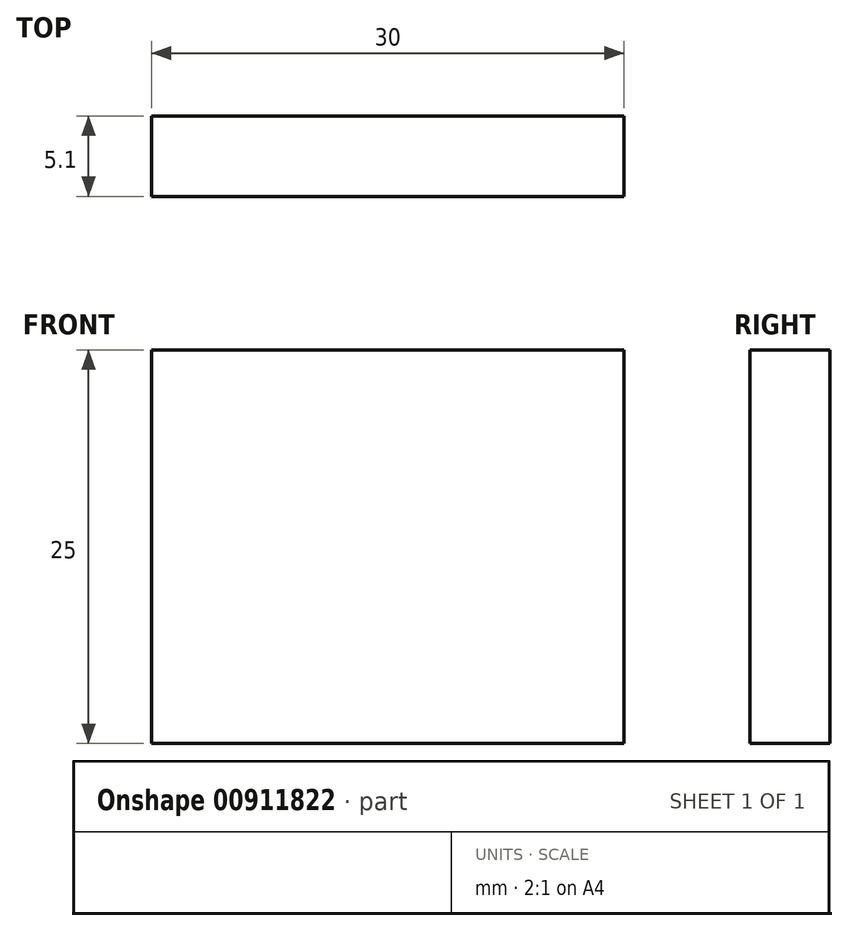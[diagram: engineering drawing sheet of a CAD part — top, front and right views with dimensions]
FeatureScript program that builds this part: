
annotation { "Feature Type Name" : "Feature", "Feature Type Description" : "" }
export const myFeature = defineFeature(function(context is Context, id is Id, definition is map)
    precondition{}
    {
        {
            var Q0;
            Q0=qCreatedBy(makeId("Front.planeOp"),FACE);
            var sketch = newSketch(context, id + "F0", { "sketchPlane" : qUnion([Q0])});
            skLineSegment(sketch, "E0.bottom", {"start": v(-78.93, 62.1) * mm, "end": v(78.93, 62.1) * mm});
            skLineSegment(sketch, "E0.top", {"start": v(-78.93, -62.1) * mm, "end": v(78.93, -62.1) * mm});
            skLineSegment(sketch, "E0.left", {"start": v(-78.93, 62.1) * mm, "end": v(-78.93, -62.1) * mm});
            skLineSegment(sketch, "E0.right", {"start": v(78.93, 62.1) * mm, "end": v(78.93, -62.1) * mm});
            skPoint(sketch, "E0.middle", {"position": v(0, 0) * mm});
            skLineSegment(sketch, "E1.bottom", {"start": v(-167.5, 20) * mm, "end": v(-136.12, 20) * mm});
            skLineSegment(sketch, "E1.top", {"start": v(-167.5, 0) * mm, "end": v(-136.12, 0) * mm});
            skLineSegment(sketch, "E1.left", {"start": v(-167.5, 20) * mm, "end": v(-167.5, 0) * mm});
            skLineSegment(sketch, "E1.right", {"start": v(-136.12, 20) * mm, "end": v(-136.12, 0) * mm});
            skLineSegment(sketch, "E2", {"start": v(-151.81, 20) * mm, "end": v(-151.81, 15) * mm});
            skLineSegment(sketch, "E3", {"start": v(-151.81, 15) * mm, "end": v(-146.81, 15) * mm});
            skLineSegment(sketch, "E4.bottom", {"start": v(-146.81, 15) * mm, "end": v(-151.81, 15) * mm});
            skLineSegment(sketch, "E4.top", {"start": v(-146.81, 5) * mm, "end": v(-151.81, 5) * mm});
            skLineSegment(sketch, "E4.left", {"start": v(-146.81, 15) * mm, "end": v(-146.81, 5) * mm});
            skPoint(sketch, "E5.end.orphan", {"position": v(-146.81, 10) * mm});
            skPoint(sketch, "E6.orphan", {"position": v(-151.81, 10) * mm});
            skPoint(sketch, "E7.end.orphan", {"position": v(-151.81, 0) * mm});
            skLineSegment(sketch, "E8", {"start": v(-151.81, 5) * mm, "end": v(-151.81, 0) * mm});
            skLineSegment(sketch, "E9.right", {"start": v(-134.62, -22.1) * mm, "end": v(-134.62, -42.1) * mm});
            skLineSegment(sketch, "E10", {"start": v(-150.31, -22.1) * mm, "end": v(-150.31, -27.1) * mm});
            skLineSegment(sketch, "E11", {"start": v(-150.31, -27.1) * mm, "end": v(-145.31, -27.1) * mm});
            skLineSegment(sketch, "E12.bottom", {"start": v(-145.31, -27.1) * mm, "end": v(-150.31, -27.1) * mm});
            skLineSegment(sketch, "E12.top", {"start": v(-145.31, -37.1) * mm, "end": v(-150.31, -37.1) * mm});
            skLineSegment(sketch, "E12.left", {"start": v(-145.31, -27.1) * mm, "end": v(-145.31, -37.1) * mm});
            skPoint(sketch, "E13.end.orphan", {"position": v(-145.31, -32.1) * mm});
            skPoint(sketch, "E14.orphan", {"position": v(-150.31, -32.1) * mm});
            skPoint(sketch, "E15.end.orphan", {"position": v(-150.31, -42.1) * mm});
            skLineSegment(sketch, "E16", {"start": v(-150.31, -37.1) * mm, "end": v(-150.31, -42.1) * mm});
            skLineSegment(sketch, "E17.left", {"start": v(-222.13, -12.84) * mm, "end": v(-222.13, -32.84) * mm});
            skLineSegment(sketch, "E18", {"start": v(-206.43, -12.84) * mm, "end": v(-206.43, -17.84) * mm});
            skLineSegment(sketch, "E19", {"start": v(-206.43, -17.84) * mm, "end": v(-201.43, -17.84) * mm});
            skLineSegment(sketch, "E20.bottom", {"start": v(-201.43, -17.84) * mm, "end": v(-206.43, -17.84) * mm});
            skLineSegment(sketch, "E20.top", {"start": v(-201.43, -27.84) * mm, "end": v(-206.43, -27.84) * mm});
            skLineSegment(sketch, "E20.left", {"start": v(-201.43, -17.84) * mm, "end": v(-201.43, -27.84) * mm});
            skPoint(sketch, "E21.end.orphan", {"position": v(-201.43, -22.84) * mm});
            skPoint(sketch, "E22.orphan", {"position": v(-206.43, -22.84) * mm});
            skPoint(sketch, "E23.end.orphan", {"position": v(-206.43, -32.84) * mm});
            skLineSegment(sketch, "E24", {"start": v(-206.43, -27.84) * mm, "end": v(-206.43, -32.84) * mm});
            skLineSegment(sketch, "E25", {"start": v(-222.13, -12.84) * mm, "end": v(-206.43, -12.84) * mm});
            skLineSegment(sketch, "E26", {"start": v(-206.43, -32.84) * mm, "end": v(-222.13, -32.84) * mm});
            skLineSegment(sketch, "E27", {"start": v(-150.31, -22.1) * mm, "end": v(-134.62, -22.1) * mm});
            skLineSegment(sketch, "E28", {"start": v(-150.31, -42.1) * mm, "end": v(-134.62, -42.1) * mm});
            skLineSegment(sketch, "E29.bottom", {"start": v(106.34, 17.4) * mm, "end": v(136.34, 17.4) * mm});
            skLineSegment(sketch, "E29.top", {"start": v(106.34, -7.6) * mm, "end": v(136.34, -7.6) * mm});
            skLineSegment(sketch, "E29.left", {"start": v(106.34, 17.4) * mm, "end": v(106.34, -7.6) * mm});
            skLineSegment(sketch, "E29.right", {"start": v(136.34, 17.4) * mm, "end": v(136.34, -7.6) * mm});
            skSolve(sketch);
        }
        {
            var Q0;
            Q0=makeQuery(id+"F0.imprint","IMPRINT",FACE,{"disambiguationData":[TD([[makeQuery(id+"F0.imprint","IMPRINT",EDGE,{"derivedFrom":sQuery(id+"F0.wireOp",EDGE,"E29.bottom")}),-1.0]])]});
            extrude(context, id + "F1", {"entities" : qUnion([Q0]), "depth" : 5.1 * mm, "offsetDistance" : 25 * mm});
        }
    });
